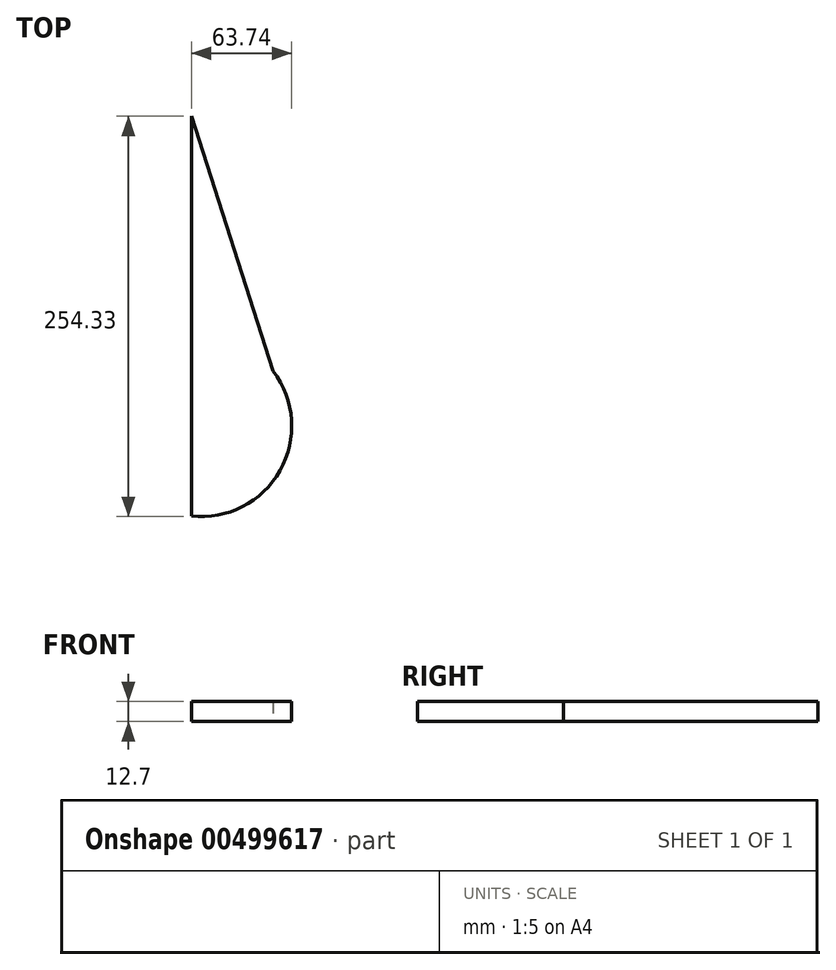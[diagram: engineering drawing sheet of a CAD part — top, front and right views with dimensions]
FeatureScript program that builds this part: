
annotation { "Feature Type Name" : "Feature", "Feature Type Description" : "" }
export const myFeature = defineFeature(function(context is Context, id is Id, definition is map)
    precondition{}
    {
        {
            var Q0;
            Q0=qCreatedBy(makeId("Top.planeOp"),FACE);
            var sketch = newSketch(context, id + "F0", { "sketchPlane" : qUnion([Q0])});
            skLineSegment(sketch, "E0", {"start": v(0, 0) * mm, "end": v(0, 254) * mm});
            skLineSegment(sketch, "E1", {"start": v(0, 254) * mm, "end": v(51.98, 92.12) * mm});
            skArc(sketch, "E2", {"start": v(0, 0) * mm, "mid": v(56.31, 28.95) * mm, "end": v(51.98, 92.12) * mm});
            skSolve(sketch);
        }
        {
            var Q0;
            Q0=makeQuery(id+"F0.imprint","IMPRINT",FACE,{"disambiguationData":[TD([[makeQuery(id+"F0.imprint","IMPRINT",EDGE,{"derivedFrom":sQuery(id+"F0.wireOp",EDGE,"E0")}),-1.0]])]});
            extrude(context, id + "F1", {"entities" : qUnion([Q0]), "depth" : 12.7 * mm});
        }
    });
